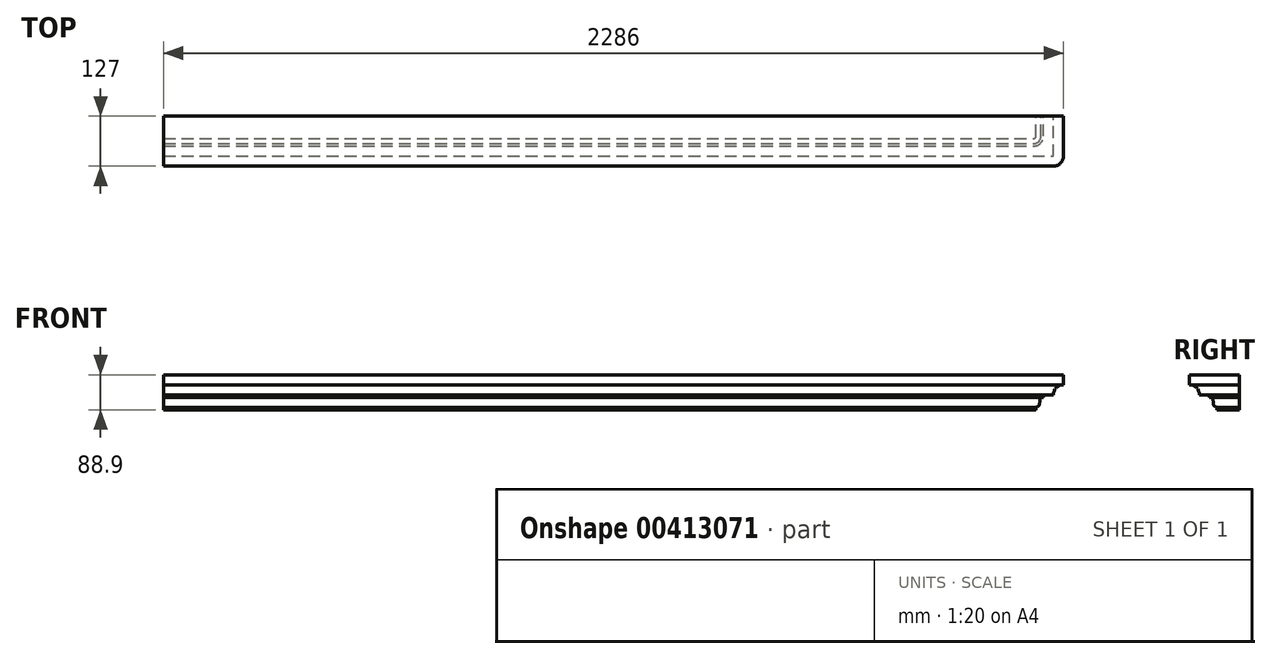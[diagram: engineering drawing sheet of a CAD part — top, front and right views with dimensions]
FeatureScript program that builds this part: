
annotation { "Feature Type Name" : "Feature", "Feature Type Description" : "" }
export const myFeature = defineFeature(function(context is Context, id is Id, definition is map)
    precondition{}
    {
        {
            var Q0;
            Q0=qCreatedBy(makeId("Front.planeOp"),FACE);
            var sketch = newSketch(context, id + "F0", { "sketchPlane" : qUnion([Q0])});
            skLineSegment(sketch, "E0.bottom", {"start": v(-1117.6, 38.1) * mm, "end": v(1117.6, 38.1) * mm});
            skLineSegment(sketch, "E0.top", {"start": v(-1117.6, 0) * mm, "end": v(1117.6, 0) * mm});
            skLineSegment(sketch, "E0.left", {"start": v(-1117.6, 38.1) * mm, "end": v(-1117.6, 0) * mm});
            skLineSegment(sketch, "E0.right", {"start": v(1117.6, 38.1) * mm, "end": v(1117.6, 0) * mm});
            skSolve(sketch);
        }
        {
            var Q0;
            Q0 = qSketchRegion(id + "F0", true);
            extrude(context, id + "F1", {"entities" : qUnion([Q0]), "depth" : 76.2 * mm});
        }
        {
            var Q0;
            Q0=makeQuery(id+"F1.opExtrude","CAP_EDGE",EDGE,{"disambiguationData":[OSD([sQuery(id+"F0.wireOp",EDGE,"E0.right")])],"isStart":false});
            fillet(context, id + "F2", {"entities" : qUnion([Q0]), "radius" : 25.4 * mm, "tangentPropagation" : true, "allowEdgeOverflow" : false});
        }
        {
            var Q0;
            Q0=makeQuery(id+"F1.opExtrude","SWEPT_FACE",FACE,{"disambiguationData":[OSD([sQuery(id+"F0.wireOp",EDGE,"E0.left")])]});
            var sketch = newSketch(context, id + "F3", { "sketchPlane" : qUnion([Q0])});
            skLineSegment(sketch, "E1", {"start": v(57.15, 0) * mm, "end": v(57.15, 6.35) * mm});
            skLineSegment(sketch, "E2", {"start": v(69.85, 31.75) * mm, "end": v(76.2, 31.75) * mm});
            skLineSegment(sketch, "E3", {"start": v(76.2, 31.75) * mm, "end": v(76.2, 0) * mm});
            skLineSegment(sketch, "E4", {"start": v(76.2, 0) * mm, "end": v(57.15, 0) * mm});
            skFitSpline(sketch, "E5", {"points": [v(57.15, 6.35) * mm, v(69.85, 31.75) * mm], "startDerivative": vector(47.96, 9.95) * mm, "endDerivative": vector(23.09, 19.63) * mm});
            skSolve(sketch);
        }
        {
            var Q0;
            Q0 = qSketchRegion(id + "F3", true);
            var Q1;
            Q1=makeQuery(id+"F1.opExtrude","CAP_EDGE",EDGE,{"disambiguationData":[OSD([sQuery(id+"F0.wireOp",EDGE,"E0.top")])],"isStart":false});
            var Q2;
            Q2=makeQuery(id+"F2.opFillet","BLEND_EDGE",EDGE,{"blendedFrom":[makeQuery(id+"F1.opExtrude","CAP_EDGE",EDGE,{"disambiguationData":[OSD([sQuery(id+"F0.wireOp",EDGE,"E0.right")])],"isStart":false}),makeQuery(id+"F1.opExtrude","SWEPT_FACE",FACE,{"disambiguationData":[OSD([sQuery(id+"F0.wireOp",EDGE,"E0.top")])]})],"blendedInto":[makeQuery(id+"F1.opExtrude","SWEPT_FACE",FACE,{"disambiguationData":[OSD([sQuery(id+"F0.wireOp",EDGE,"E0.top")])]})]});
            var Q3;
            Q3=makeQuery(id+"F1.opExtrude","SWEPT_EDGE",EDGE,{"disambiguationData":[OSD([sQuery(id+"F0.wireOp",EDGE,"E0.top"),sQuery(id+"F0.wireOp",EDGE,"E0.right")])]});
            sweep(context, id + "F4", {"operationType" : NewBodyOperationType.REMOVE, "profiles" : qUnion([Q0]), "path" : qUnion([Q1, Q2, Q3])});
        }
        {
            var Q0;
            Q0=makeQuery(id+"F1.opExtrude","SWEPT_FACE",FACE,{"disambiguationData":[OSD([sQuery(id+"F0.wireOp",EDGE,"E0.bottom")])]});
            var sketch = newSketch(context, id + "F5", { "sketchPlane" : qUnion([Q0])});
            skLineSegment(sketch, "E6.bottom", {"start": v(-1117.6, 0) * mm, "end": v(1168.4, 0) * mm});
            skLineSegment(sketch, "E6.top", {"start": v(-1117.6, -127) * mm, "end": v(1168.4, -127) * mm});
            skLineSegment(sketch, "E6.left", {"start": v(-1117.6, 0) * mm, "end": v(-1117.6, -127) * mm});
            skLineSegment(sketch, "E6.right", {"start": v(1168.4, 0) * mm, "end": v(1168.4, -127) * mm});
            skLineSegment(sketch, "E7", {"start": v(1117.6, -25.4) * mm, "end": v(1168.4, -25.4) * mm, "construction": true});
            skLineSegment(sketch, "E8", {"start": v(895.06, -76.2) * mm, "end": v(895.06, -127) * mm, "construction": true});
            skSolve(sketch);
        }
        {
            var Q0;
            Q0 = qSketchRegion(id + "F5", true);
            extrude(context, id + "F6", {"entities" : qUnion([Q0]), "operationType" : NewBodyOperationType.ADD, "depth" : 50.8 * mm});
        }
        {
            var Q0;
            Q0=makeQuery(id+"F6.opExtrude","SWEPT_EDGE",EDGE,{"disambiguationData":[OSD([sQuery(id+"F5.wireOp",EDGE,"E6.top"),sQuery(id+"F5.wireOp",EDGE,"E6.right")])]});
            fillet(context, id + "F7", {"entities" : qUnion([Q0]), "radius" : 25.4 * mm, "tangentPropagation" : true, "allowEdgeOverflow" : false});
        }
        {
            var Q0;
            Q0=makeQuery(id+"F6.boolean.opBoolean","MERGE",FACE,{"derivedFrom":[makeQuery(id+"F1.opExtrude","SWEPT_FACE",FACE,{"disambiguationData":[OSD([sQuery(id+"F0.wireOp",EDGE,"E0.left")])]}),makeQuery(id+"F6.opExtrude","SWEPT_FACE",FACE,{"disambiguationData":[OSD([sQuery(id+"F5.wireOp",EDGE,"E6.left")])]})]});
            var sketch = newSketch(context, id + "F8", { "sketchPlane" : qUnion([Q0])});
            skCircle(sketch, "E9", {"center": v(127, 38.1) * mm, "radius": 25.4 * mm});
            skSolve(sketch);
        }
        {
            var Q0;
            Q0 = qSketchRegion(id + "F8", true);
            var Q1;
            Q1=makeQuery(id+"F6.opExtrude","CAP_EDGE",EDGE,{"disambiguationData":[OSD([sQuery(id+"F5.wireOp",EDGE,"E6.top")])],"isStart":true});
            var Q2;
            {var subQ0=sQuery(id+"F5.wireOp",EDGE,"E6.right");var subQ1=sQuery(id+"F5.wireOp",EDGE,"E6.top");Q2=makeQuery(id+"F7.opFillet","BLEND_EDGE",EDGE,{"blendedFrom":[makeQuery(id+"F6.opExtrude","SWEPT_EDGE",EDGE,{"disambiguationData":[OSD([subQ1,subQ0])]}),makeQuery(id+"F6.opExtrude","CAP_FACE",FACE,{"disambiguationData":[OSD([sQuery(id+"F5.wireOp",EDGE,"E6.bottom"),subQ1,sQuery(id+"F5.wireOp",EDGE,"E6.left"),subQ0])],"isStart":true})],"blendedInto":[makeQuery(id+"F6.opExtrude","CAP_FACE",FACE,{"disambiguationData":[OSD([sQuery(id+"F5.wireOp",EDGE,"E6.bottom"),subQ1,sQuery(id+"F5.wireOp",EDGE,"E6.left"),subQ0])],"isStart":true})]});}
            var Q3;
            Q3=makeQuery(id+"F6.opExtrude","CAP_EDGE",EDGE,{"disambiguationData":[OSD([sQuery(id+"F5.wireOp",EDGE,"E6.right")])],"isStart":true});
            sweep(context, id + "F9", {"operationType" : NewBodyOperationType.REMOVE, "profiles" : qUnion([Q0]), "path" : qUnion([Q1, Q2, Q3])});
        }
    });
